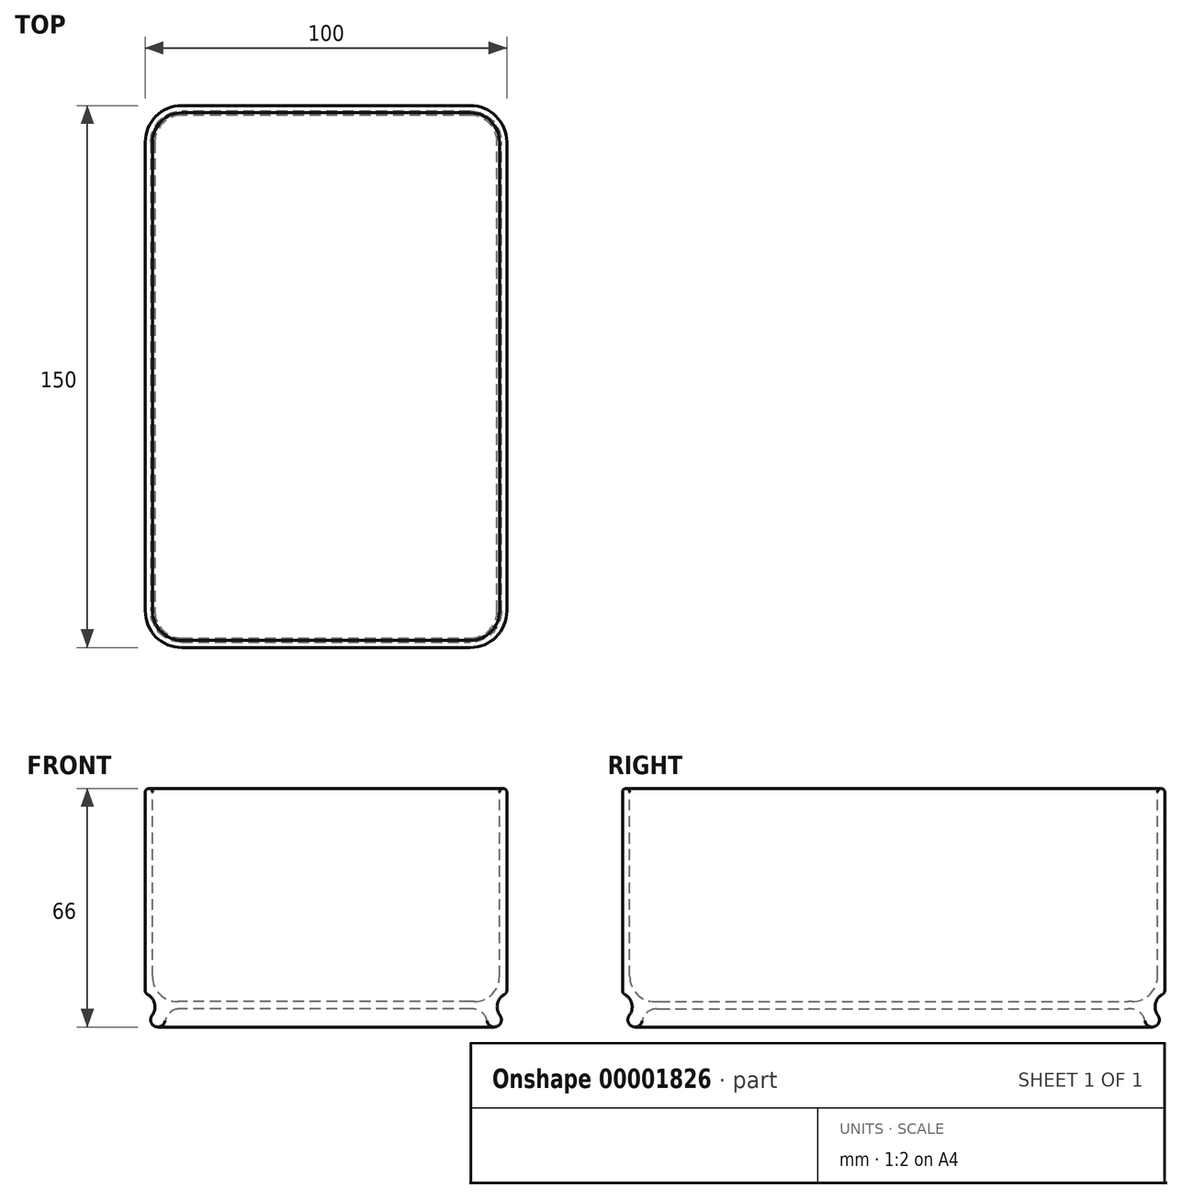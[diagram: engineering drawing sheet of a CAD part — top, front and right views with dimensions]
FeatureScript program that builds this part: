
annotation { "Feature Type Name" : "Feature", "Feature Type Description" : "" }
export const myFeature = defineFeature(function(context is Context, id is Id, definition is map)
    precondition{}
    {
        {
            var Q0;
            Q0=qCreatedBy(makeId("Top.planeOp"),FACE);
            var sketch = newSketch(context, id + "F0", { "sketchPlane" : qUnion([Q0])});
            skLineSegment(sketch, "E0", {"start": v(-126.71, 0) * mm, "end": v(114.49, 0) * mm, "construction": true});
            skLineSegment(sketch, "E1", {"start": v(0, 107.71) * mm, "end": v(0, -93.3) * mm, "construction": true});
            skLineSegment(sketch, "E2", {"start": v(0, 65) * mm, "end": v(-39.9, 65) * mm});
            skLineSegment(sketch, "E3", {"start": v(-40, 64.9) * mm, "end": v(-40, 0) * mm});
            skPoint(sketch, "E4.visualSharp", {"position": v(-40, 65) * mm});
            skArc(sketch, "E4.filletArc", {"start": v(-39.9, 65) * mm, "mid": v(-39.97, 64.97) * mm, "end": v(-40, 64.9) * mm});
            skLineSegment(sketch, "E5.0.MirrorCS", {"start": v(0, 65) * mm, "end": v(39.9, 65) * mm});
            skArc(sketch, "E6.0.MirrorCS", {"start": v(39.9, 65) * mm, "mid": v(39.97, 64.97) * mm, "end": v(40, 64.9) * mm});
            skLineSegment(sketch, "E7.0.MirrorCS", {"start": v(40, 64.9) * mm, "end": v(40, 0) * mm});
            skLineSegment(sketch, "E8.0.MirrorCS", {"start": v(0, -65) * mm, "end": v(39.9, -65) * mm});
            skLineSegment(sketch, "E8.1.MirrorCS", {"start": v(40, -64.9) * mm, "end": v(40, 0) * mm});
            skLineSegment(sketch, "E8.2.MirrorCS", {"start": v(0, -65) * mm, "end": v(-39.9, -65) * mm});
            skLineSegment(sketch, "E8.3.MirrorCS", {"start": v(-40, -64.9) * mm, "end": v(-40, 0) * mm});
            skArc(sketch, "E8.4.MirrorCS", {"start": v(-39.9, -65) * mm, "mid": v(-39.97, -64.97) * mm, "end": v(-40, -64.9) * mm});
            skPoint(sketch, "E8.5.MirrorP", {"position": v(-40, -65) * mm});
            skArc(sketch, "E8.6.MirrorCS", {"start": v(39.9, -65) * mm, "mid": v(39.97, -64.97) * mm, "end": v(40, -64.9) * mm});
            skSolve(sketch);
        }
        {
            var Q0;
            Q0=makeQuery(id+"F0.imprint","IMPRINT",FACE,{"disambiguationData":[TD([[makeQuery(id+"F0.imprint","IMPRINT",EDGE,{"derivedFrom":sQuery(id+"F0.wireOp",EDGE,"E3")}),1.0]])]});
            var Q1;
            Q1=makeQuery(id+"F3.opSweep","SWEPT_BODY",BODY,{"disambiguationData":[OSD([sQuery(id+"F0.wireOp",EDGE,"E2"),sQuery(id+"F2.wireOp",EDGE,"E11"),sQuery(id+"F2.wireOp",EDGE,"E12"),sQuery(id+"F2.wireOp",EDGE,"E14"),sQuery(id+"F2.wireOp",EDGE,"ab67ea49-341e-467c-9989-4a48574b13ad"),sQuery(id+"F2.wireOp",EDGE,"E15.filletArc"),sQuery(id+"F2.wireOp",EDGE,"E16.filletArc")])]});
            extrude(context, id + "F1", {"entities" : qUnion([Q0]), "endBoundEntity" : qUnion([Q1]), "depth" : 2 * mm});
        }
        {
            var Q0;
            Q0=qCreatedBy(makeId("Front.planeOp"),FACE);
            var sketch = newSketch(context, id + "F2", { "sketchPlane" : qUnion([Q0])});
            skLineSegment(sketch, "E9", {"start": v(-50, 34.05) * mm, "end": v(-50, -49.06) * mm, "construction": true});
            skLineSegment(sketch, "E10", {"start": v(-51.91, 60) * mm, "end": v(-36.31, 60) * mm, "construction": true});
            skLineSegment(sketch, "E11", {"start": v(-50, 60) * mm, "end": v(-50, 5) * mm});
            skLineSegment(sketch, "E12", {"start": v(-40, 0) * mm, "end": v(-40, 2) * mm});
            skLineSegment(sketch, "E13", {"start": v(-40, 2) * mm, "end": v(-41, 2) * mm});
            skLineSegment(sketch, "E14", {"start": v(-48, 9) * mm, "end": v(-48, 60) * mm});
            skPoint(sketch, "E15.visualSharp", {"position": v(-48, 2) * mm});
            skArc(sketch, "E15.filletArc", {"start": v(-48, 9) * mm, "mid": v(-45.95, 4.05) * mm, "end": v(-41, 2) * mm});
            skArc(sketch, "E16.filletArc", {"start": v(-50, 5) * mm, "mid": v(-49.86, 4.48) * mm, "end": v(-49.46, 4.11) * mm});
            skArc(sketch, "E17", {"start": v(-49.46, 4.11) * mm, "mid": v(-47.42, 1.46) * mm, "end": v(-48.1, -1.8) * mm});
            skArc(sketch, "E18", {"start": v(-48.1, -1.8) * mm, "mid": v(-47.28, -4.84) * mm, "end": v(-44.53, -3.33) * mm});
            skArc(sketch, "E19", {"start": v(-44.53, -3.33) * mm, "mid": v(-43.17, -0.94) * mm, "end": v(-40.58, 0) * mm});
            skLineSegment(sketch, "E20", {"start": v(-40.58, 0) * mm, "end": v(-40, 0) * mm});
            skArc(sketch, "E21", {"start": v(-48, 60) * mm, "mid": v(-49, 61) * mm, "end": v(-50, 60) * mm});
            skLineSegment(sketch, "E22", {"start": v(-48, 0) * mm, "end": v(-48, -10.54) * mm, "construction": true});
            skCircle(sketch, "E23", {"center": v(-49, 2.47) * mm, "radius": 1 * mm, "construction": true});
            skSolve(sketch);
        }
        {
            var Q0;
            Q0=makeQuery(id+"F2.imprint","IMPRINT",FACE,{"disambiguationData":[TD([[makeQuery(id+"F2.imprint","IMPRINT",EDGE,{"derivedFrom":sQuery(id+"F2.wireOp",EDGE,"E11")}),1.0]])]});
            var Q1;
            Q1=sQuery(id+"F0.wireOp",EDGE,"E3");
            var Q2;
            Q2=sQuery(id+"F0.wireOp",EDGE,"E4.filletArc");
            var Q3;
            Q3=sQuery(id+"F0.wireOp",EDGE,"E2");
            var Q4;
            Q4=sQuery(id+"F0.wireOp",EDGE,"E5.0.MirrorCS");
            var Q5;
            Q5=sQuery(id+"F0.wireOp",EDGE,"E6.0.MirrorCS");
            var Q6;
            Q6=sQuery(id+"F0.wireOp",EDGE,"E7.0.MirrorCS");
            var Q7;
            Q7=sQuery(id+"F0.wireOp",EDGE,"E8.1.MirrorCS");
            var Q8;
            Q8=sQuery(id+"F0.wireOp",EDGE,"E8.6.MirrorCS");
            var Q9;
            Q9=sQuery(id+"F0.wireOp",EDGE,"E8.0.MirrorCS");
            var Q10;
            Q10=sQuery(id+"F0.wireOp",EDGE,"E8.2.MirrorCS");
            var Q11;
            Q11=sQuery(id+"F0.wireOp",EDGE,"E8.4.MirrorCS");
            var Q12;
            Q12=sQuery(id+"F0.wireOp",EDGE,"E8.3.MirrorCS");
            sweep(context, id + "F3", {"operationType" : NewBodyOperationType.ADD, "profiles" : qUnion([Q0]), "path" : qUnion([Q1, Q2, Q3, Q4, Q5, Q6, Q7, Q8, Q9, Q10, Q11, Q12])});
        }
    });
